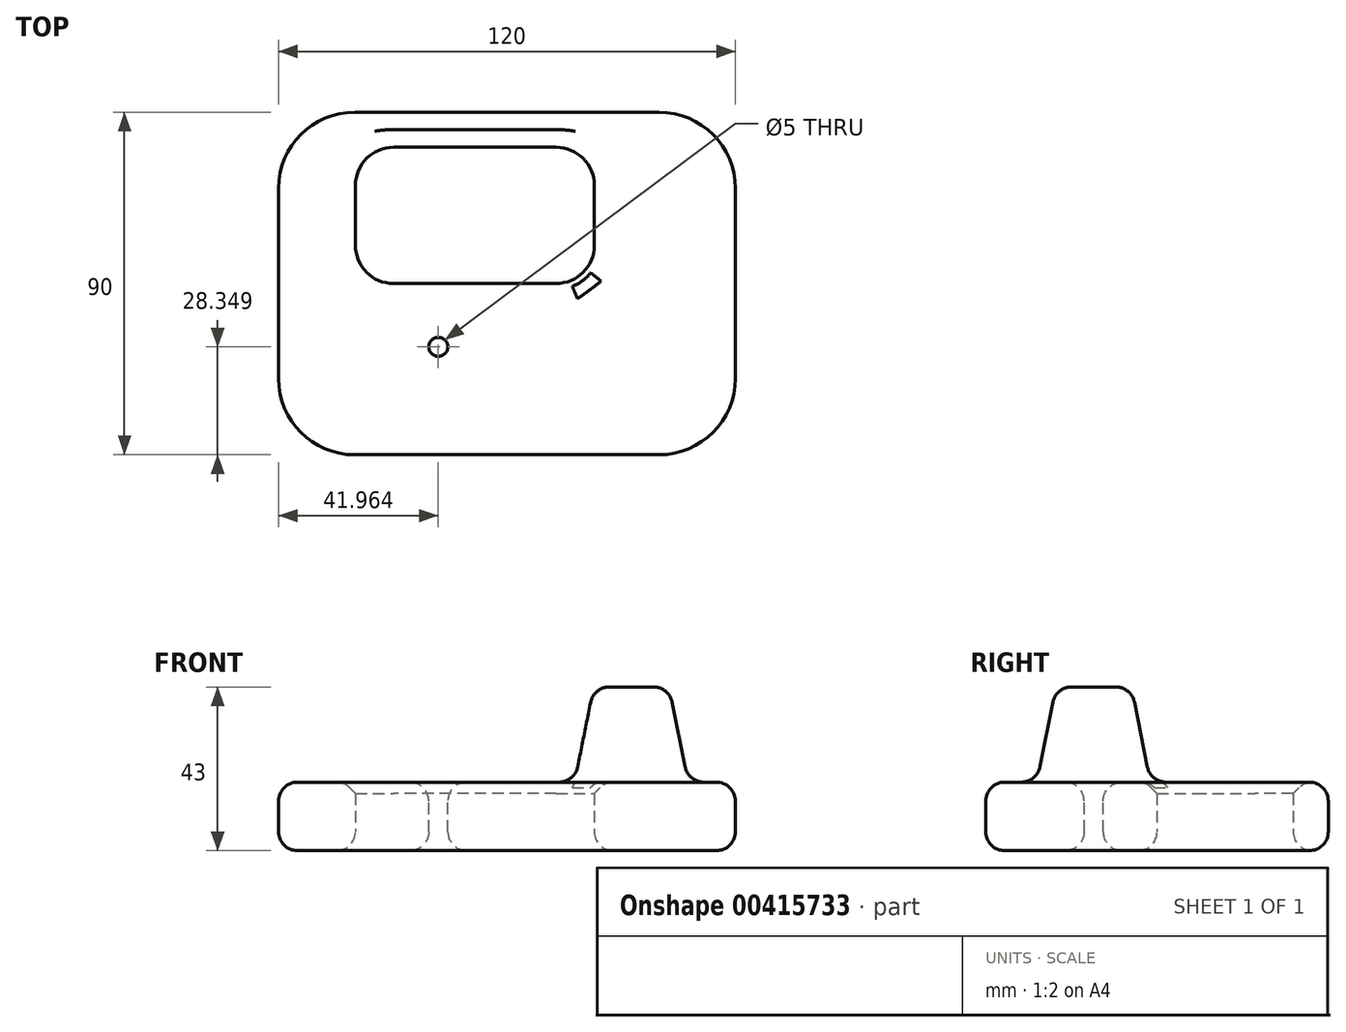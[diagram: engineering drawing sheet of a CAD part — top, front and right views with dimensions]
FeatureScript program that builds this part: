
annotation { "Feature Type Name" : "Feature", "Feature Type Description" : "" }
export const myFeature = defineFeature(function(context is Context, id is Id, definition is map)
    precondition{}
    {
        {
            var Q0;
            Q0=qCreatedBy(makeId("Top.planeOp"),FACE);
            var sketch = newSketch(context, id + "F0", { "sketchPlane" : qUnion([Q0])});
            skLineSegment(sketch, "E0.bottom", {"start": v(60, 45) * mm, "end": v(-60, 45) * mm});
            skLineSegment(sketch, "E0.top", {"start": v(60, -45) * mm, "end": v(-60, -45) * mm});
            skLineSegment(sketch, "E0.left", {"start": v(60, 45) * mm, "end": v(60, -45) * mm});
            skLineSegment(sketch, "E0.right", {"start": v(-60, 45) * mm, "end": v(-60, -45) * mm});
            skPoint(sketch, "E0.middle", {"position": v(0, 0) * mm});
            skSolve(sketch);
        }
        {
            var Q0;
            Q0=makeQuery(id+"F0.imprint","IMPRINT",FACE,{"disambiguationData":[TD([[makeQuery(id+"F0.imprint","IMPRINT",EDGE,{"derivedFrom":sQuery(id+"F0.wireOp",EDGE,"E0.bottom")}),1.0]])]});
            extrude(context, id + "F1", {"entities" : qUnion([Q0]), "depth" : 18 * mm});
        }
        {
            var Q0;
            Q0=qCreatedBy(makeId("Top.planeOp"),FACE);
            var sketch = newSketch(context, id + "F2", { "sketchPlane" : qUnion([Q0])});
            skLineSegment(sketch, "E1.bottom", {"start": v(22.95, 35.77) * mm, "end": v(-39.8, 35.77) * mm});
            skLineSegment(sketch, "E1.top", {"start": v(22.95, 0) * mm, "end": v(-39.8, 0) * mm});
            skLineSegment(sketch, "E1.left", {"start": v(22.95, 35.77) * mm, "end": v(22.95, 0) * mm});
            skLineSegment(sketch, "E1.right", {"start": v(-39.8, 35.77) * mm, "end": v(-39.8, 0) * mm});
            skSolve(sketch);
        }
        {
            var Q0;
            Q0=makeQuery(id+"F1.opExtrude","CAP_FACE",FACE,{"disambiguationData":[OSD([sQuery(id+"F0.wireOp",EDGE,"E0.bottom"),sQuery(id+"F0.wireOp",EDGE,"E0.top"),sQuery(id+"F0.wireOp",EDGE,"E0.left"),sQuery(id+"F0.wireOp",EDGE,"E0.right")])],"isStart":false});
            var Q1;
            Q1=makeQuery(id+"F2.imprint","IMPRINT",FACE,{"disambiguationData":[TD([[makeQuery(id+"F2.imprint","IMPRINT",EDGE,{"derivedFrom":sQuery(id+"F2.wireOp",EDGE,"E1.bottom")}),1.0]])]});
            extrude(context, id + "F3", {"entities" : qUnion([Q0, Q1]), "operationType" : NewBodyOperationType.REMOVE, "depth" : 20 * mm});
        }
        {
            var Q0;
            Q0=makeQuery(id+"F3.boolean.opBoolean","COPY",EDGE,{"derivedFrom":makeQuery(id+"F3.opExtrude","SWEPT_EDGE",EDGE,{"disambiguationData":[OSD([sQuery(id+"F2.wireOp",EDGE,"E1.bottom"),sQuery(id+"F2.wireOp",EDGE,"E1.left")])]})});
            var Q1;
            {var subQ0=sQuery(id+"F0.wireOp",EDGE,"E0.right");var subQ1=sQuery(id+"F0.wireOp",EDGE,"E0.left");var subQ2=sQuery(id+"F0.wireOp",EDGE,"E0.top");var subQ3=sQuery(id+"F0.wireOp",EDGE,"E0.bottom");var subQ4=makeQuery(id+"F1.opExtrude","CAP_FACE",FACE,{"disambiguationData":[OSD([subQ3,subQ2,subQ1,subQ0])],"isStart":false});var subQ5=makeQuery(id+"F3.opExtrude","CAP_FACE",FACE,{"disambiguationData":[OSD([subQ3,subQ2,subQ1,subQ0])],"isStart":true});Q1=makeQuery(id+"FmhjPb4m4sN7J4q_1.opFillet","BLEND_EDGE",EDGE,{"blendedFrom":[makeQuery(id+"F3.boolean.opBoolean","INTERSECT",EDGE,{"disambiguationData":[topologyDisambiguationEdgeConnected([makeQuery(id+"F3.opExtrude","SWEPT_FACE",FACE,{"disambiguationData":[OSD([sQuery(id+"F2.wireOp",EDGE,"E1.bottom")])]})])],"derivedFrom":[subQ4,subQ5]}),makeQuery(id+"F3.boolean.opBoolean","INTERSECT",EDGE,{"disambiguationData":[topologyDisambiguationEdgeConnected([makeQuery(id+"F3.opExtrude","SWEPT_FACE",FACE,{"disambiguationData":[OSD([sQuery(id+"F2.wireOp",EDGE,"E1.left")])]})])],"derivedFrom":[subQ4,subQ5]})],"blendedInto":[]});}
            var Q2;
            Q2=makeQuery(id+"F3.boolean.opBoolean","COPY",EDGE,{"derivedFrom":makeQuery(id+"F3.opExtrude","SWEPT_EDGE",EDGE,{"disambiguationData":[OSD([sQuery(id+"F2.wireOp",EDGE,"E1.bottom"),sQuery(id+"F2.wireOp",EDGE,"E1.right")])]})});
            var Q3;
            {var subQ0=sQuery(id+"F0.wireOp",EDGE,"E0.right");var subQ1=sQuery(id+"F0.wireOp",EDGE,"E0.left");var subQ2=sQuery(id+"F0.wireOp",EDGE,"E0.top");var subQ3=sQuery(id+"F0.wireOp",EDGE,"E0.bottom");var subQ4=makeQuery(id+"F1.opExtrude","CAP_FACE",FACE,{"disambiguationData":[OSD([subQ3,subQ2,subQ1,subQ0])],"isStart":false});var subQ5=makeQuery(id+"F3.opExtrude","CAP_FACE",FACE,{"disambiguationData":[OSD([subQ3,subQ2,subQ1,subQ0])],"isStart":true});Q3=makeQuery(id+"FmhjPb4m4sN7J4q_1.opFillet","BLEND_EDGE",EDGE,{"blendedFrom":[makeQuery(id+"F3.boolean.opBoolean","INTERSECT",EDGE,{"disambiguationData":[topologyDisambiguationEdgeConnected([makeQuery(id+"F3.opExtrude","SWEPT_FACE",FACE,{"disambiguationData":[OSD([sQuery(id+"F2.wireOp",EDGE,"E1.bottom")])]})])],"derivedFrom":[subQ4,subQ5]}),makeQuery(id+"F3.boolean.opBoolean","INTERSECT",EDGE,{"disambiguationData":[topologyDisambiguationEdgeConnected([makeQuery(id+"F3.opExtrude","SWEPT_FACE",FACE,{"disambiguationData":[OSD([sQuery(id+"F2.wireOp",EDGE,"E1.right")])]})])],"derivedFrom":[subQ4,subQ5]})],"blendedInto":[]});}
            var Q4;
            Q4=makeQuery(id+"F3.boolean.opBoolean","COPY",EDGE,{"derivedFrom":makeQuery(id+"F3.opExtrude","SWEPT_EDGE",EDGE,{"disambiguationData":[OSD([sQuery(id+"F2.wireOp",EDGE,"E1.top"),sQuery(id+"F2.wireOp",EDGE,"E1.right")])]})});
            var Q5;
            {var subQ0=sQuery(id+"F0.wireOp",EDGE,"E0.right");var subQ1=sQuery(id+"F0.wireOp",EDGE,"E0.left");var subQ2=sQuery(id+"F0.wireOp",EDGE,"E0.top");var subQ3=sQuery(id+"F0.wireOp",EDGE,"E0.bottom");var subQ4=makeQuery(id+"F1.opExtrude","CAP_FACE",FACE,{"disambiguationData":[OSD([subQ3,subQ2,subQ1,subQ0])],"isStart":false});var subQ5=makeQuery(id+"F3.opExtrude","CAP_FACE",FACE,{"disambiguationData":[OSD([subQ3,subQ2,subQ1,subQ0])],"isStart":true});Q5=makeQuery(id+"FmhjPb4m4sN7J4q_1.opFillet","BLEND_EDGE",EDGE,{"blendedFrom":[makeQuery(id+"F3.boolean.opBoolean","INTERSECT",EDGE,{"disambiguationData":[topologyDisambiguationEdgeConnected([makeQuery(id+"F3.opExtrude","SWEPT_FACE",FACE,{"disambiguationData":[OSD([sQuery(id+"F2.wireOp",EDGE,"E1.top")])]})])],"derivedFrom":[subQ4,subQ5]}),makeQuery(id+"F3.boolean.opBoolean","INTERSECT",EDGE,{"disambiguationData":[topologyDisambiguationEdgeConnected([makeQuery(id+"F3.opExtrude","SWEPT_FACE",FACE,{"disambiguationData":[OSD([sQuery(id+"F2.wireOp",EDGE,"E1.right")])]})])],"derivedFrom":[subQ4,subQ5]})],"blendedInto":[]});}
            var Q6;
            Q6=makeQuery(id+"F3.boolean.opBoolean","COPY",EDGE,{"derivedFrom":makeQuery(id+"F3.opExtrude","SWEPT_EDGE",EDGE,{"disambiguationData":[OSD([sQuery(id+"F2.wireOp",EDGE,"E1.top"),sQuery(id+"F2.wireOp",EDGE,"E1.left")])]})});
            var Q7;
            {var subQ0=sQuery(id+"F0.wireOp",EDGE,"E0.right");var subQ1=sQuery(id+"F0.wireOp",EDGE,"E0.left");var subQ2=sQuery(id+"F0.wireOp",EDGE,"E0.top");var subQ3=sQuery(id+"F0.wireOp",EDGE,"E0.bottom");var subQ4=makeQuery(id+"F1.opExtrude","CAP_FACE",FACE,{"disambiguationData":[OSD([subQ3,subQ2,subQ1,subQ0])],"isStart":false});var subQ5=makeQuery(id+"F3.opExtrude","CAP_FACE",FACE,{"disambiguationData":[OSD([subQ3,subQ2,subQ1,subQ0])],"isStart":true});Q7=makeQuery(id+"FmhjPb4m4sN7J4q_1.opFillet","BLEND_EDGE",EDGE,{"blendedFrom":[makeQuery(id+"F3.boolean.opBoolean","INTERSECT",EDGE,{"disambiguationData":[topologyDisambiguationEdgeConnected([makeQuery(id+"F3.opExtrude","SWEPT_FACE",FACE,{"disambiguationData":[OSD([sQuery(id+"F2.wireOp",EDGE,"E1.top")])]})])],"derivedFrom":[subQ4,subQ5]}),makeQuery(id+"F3.boolean.opBoolean","INTERSECT",EDGE,{"disambiguationData":[topologyDisambiguationEdgeConnected([makeQuery(id+"F3.opExtrude","SWEPT_FACE",FACE,{"disambiguationData":[OSD([sQuery(id+"F2.wireOp",EDGE,"E1.left")])]})])],"derivedFrom":[subQ4,subQ5]})],"blendedInto":[]});}
            fillet(context, id + "F4", {"entities" : qUnion([Q0, Q1, Q2, Q3, Q4, Q5, Q6, Q7]), "radius" : 10 * mm, "tangentPropagation" : true, "allowEdgeOverflow" : false});
        }
        {
            var Q0;
            Q0=makeQuery(id+"F1.opExtrude","SWEPT_EDGE",EDGE,{"disambiguationData":[OSD([sQuery(id+"F0.wireOp",EDGE,"E0.top"),sQuery(id+"F0.wireOp",EDGE,"E0.right")])]});
            var Q1;
            Q1=makeQuery(id+"F1.opExtrude","SWEPT_EDGE",EDGE,{"disambiguationData":[OSD([sQuery(id+"F0.wireOp",EDGE,"E0.bottom"),sQuery(id+"F0.wireOp",EDGE,"E0.right")])]});
            var Q2;
            Q2=makeQuery(id+"F1.opExtrude","SWEPT_EDGE",EDGE,{"disambiguationData":[OSD([sQuery(id+"F0.wireOp",EDGE,"E0.top"),sQuery(id+"F0.wireOp",EDGE,"E0.left")])]});
            var Q3;
            Q3=makeQuery(id+"F1.opExtrude","SWEPT_EDGE",EDGE,{"disambiguationData":[OSD([sQuery(id+"F0.wireOp",EDGE,"E0.bottom"),sQuery(id+"F0.wireOp",EDGE,"E0.left")])]});
            fillet(context, id + "F5", {"entities" : qUnion([Q0, Q1, Q2, Q3]), "radius" : 20 * mm, "tangentPropagation" : true, "allowEdgeOverflow" : false});
        }
        {
            var Q0;
            {var subQ0=sQuery(id+"F0.wireOp",EDGE,"E0.right");var subQ1=sQuery(id+"F0.wireOp",EDGE,"E0.left");var subQ2=sQuery(id+"F0.wireOp",EDGE,"E0.top");var subQ3=sQuery(id+"F0.wireOp",EDGE,"E0.bottom");var subQ4=makeQuery(id+"F1.opExtrude","CAP_FACE",FACE,{"disambiguationData":[OSD([subQ3,subQ2,subQ1,subQ0])],"isStart":false});Q0=makeQuery(id+"F3.boolean.opBoolean","INTERSECT",EDGE,{"disambiguationData":[topologyDisambiguationEdgeConnected([makeQuery(id+"F3.opExtrude","SWEPT_FACE",FACE,{"disambiguationData":[OSD([sQuery(id+"F2.wireOp",EDGE,"E1.bottom")])]})])],"derivedFrom":[subQ4,makeQuery(id+"F3.opExtrude","CAP_FACE",FACE,{"disambiguationData":[OSD([subQ3,subQ2,subQ1,subQ0])],"isStart":true})]});}
            var Q1;
            Q1=makeQuery(id+"F4.opFillet","BLEND_EDGE",EDGE,{"blendedFrom":[makeQuery(id+"F3.boolean.opBoolean","COPY",EDGE,{"derivedFrom":makeQuery(id+"F3.opExtrude","SWEPT_EDGE",EDGE,{"disambiguationData":[OSD([sQuery(id+"F2.wireOp",EDGE,"E1.bottom"),sQuery(id+"F2.wireOp",EDGE,"E1.left")])]})}),makeQuery(id+"F1.opExtrude","CAP_FACE",FACE,{"disambiguationData":[OSD([sQuery(id+"F0.wireOp",EDGE,"E0.bottom"),sQuery(id+"F0.wireOp",EDGE,"E0.top"),sQuery(id+"F0.wireOp",EDGE,"E0.left"),sQuery(id+"F0.wireOp",EDGE,"E0.right")])],"isStart":false})],"blendedInto":[makeQuery(id+"F1.opExtrude","CAP_FACE",FACE,{"disambiguationData":[OSD([sQuery(id+"F0.wireOp",EDGE,"E0.bottom"),sQuery(id+"F0.wireOp",EDGE,"E0.top"),sQuery(id+"F0.wireOp",EDGE,"E0.left"),sQuery(id+"F0.wireOp",EDGE,"E0.right")])],"isStart":false})]});
            var Q2;
            {var subQ0=sQuery(id+"F0.wireOp",EDGE,"E0.right");var subQ1=sQuery(id+"F0.wireOp",EDGE,"E0.left");var subQ2=sQuery(id+"F0.wireOp",EDGE,"E0.top");var subQ3=sQuery(id+"F0.wireOp",EDGE,"E0.bottom");var subQ4=makeQuery(id+"F1.opExtrude","CAP_FACE",FACE,{"disambiguationData":[OSD([subQ3,subQ2,subQ1,subQ0])],"isStart":false});Q2=makeQuery(id+"F3.boolean.opBoolean","INTERSECT",EDGE,{"disambiguationData":[topologyDisambiguationEdgeConnected([makeQuery(id+"F3.opExtrude","SWEPT_FACE",FACE,{"disambiguationData":[OSD([sQuery(id+"F2.wireOp",EDGE,"E1.left")])]})])],"derivedFrom":[subQ4,makeQuery(id+"F3.opExtrude","CAP_FACE",FACE,{"disambiguationData":[OSD([subQ3,subQ2,subQ1,subQ0])],"isStart":true})]});}
            var Q3;
            Q3=makeQuery(id+"F4.opFillet","BLEND_EDGE",EDGE,{"blendedFrom":[makeQuery(id+"F3.boolean.opBoolean","COPY",EDGE,{"derivedFrom":makeQuery(id+"F3.opExtrude","SWEPT_EDGE",EDGE,{"disambiguationData":[OSD([sQuery(id+"F2.wireOp",EDGE,"E1.top"),sQuery(id+"F2.wireOp",EDGE,"E1.left")])]})}),makeQuery(id+"F1.opExtrude","CAP_FACE",FACE,{"disambiguationData":[OSD([sQuery(id+"F0.wireOp",EDGE,"E0.bottom"),sQuery(id+"F0.wireOp",EDGE,"E0.top"),sQuery(id+"F0.wireOp",EDGE,"E0.left"),sQuery(id+"F0.wireOp",EDGE,"E0.right")])],"isStart":false})],"blendedInto":[makeQuery(id+"F1.opExtrude","CAP_FACE",FACE,{"disambiguationData":[OSD([sQuery(id+"F0.wireOp",EDGE,"E0.bottom"),sQuery(id+"F0.wireOp",EDGE,"E0.top"),sQuery(id+"F0.wireOp",EDGE,"E0.left"),sQuery(id+"F0.wireOp",EDGE,"E0.right")])],"isStart":false})]});
            var Q4;
            {var subQ0=sQuery(id+"F0.wireOp",EDGE,"E0.right");var subQ1=sQuery(id+"F0.wireOp",EDGE,"E0.left");var subQ2=sQuery(id+"F0.wireOp",EDGE,"E0.top");var subQ3=sQuery(id+"F0.wireOp",EDGE,"E0.bottom");var subQ4=makeQuery(id+"F1.opExtrude","CAP_FACE",FACE,{"disambiguationData":[OSD([subQ3,subQ2,subQ1,subQ0])],"isStart":false});Q4=makeQuery(id+"F3.boolean.opBoolean","INTERSECT",EDGE,{"disambiguationData":[topologyDisambiguationEdgeConnected([makeQuery(id+"F3.opExtrude","SWEPT_FACE",FACE,{"disambiguationData":[OSD([sQuery(id+"F2.wireOp",EDGE,"E1.top")])]})])],"derivedFrom":[subQ4,makeQuery(id+"F3.opExtrude","CAP_FACE",FACE,{"disambiguationData":[OSD([subQ3,subQ2,subQ1,subQ0])],"isStart":true})]});}
            var Q5;
            {var subQ0=sQuery(id+"F0.wireOp",EDGE,"E0.right");var subQ1=sQuery(id+"F0.wireOp",EDGE,"E0.left");var subQ2=sQuery(id+"F0.wireOp",EDGE,"E0.top");var subQ3=sQuery(id+"F0.wireOp",EDGE,"E0.bottom");var subQ4=makeQuery(id+"F1.opExtrude","CAP_FACE",FACE,{"disambiguationData":[OSD([subQ3,subQ2,subQ1,subQ0])],"isStart":false});Q5=makeQuery(id+"F3.boolean.opBoolean","INTERSECT",EDGE,{"disambiguationData":[topologyDisambiguationEdgeConnected([makeQuery(id+"F3.opExtrude","SWEPT_FACE",FACE,{"disambiguationData":[OSD([sQuery(id+"F2.wireOp",EDGE,"E1.right")])]})])],"derivedFrom":[subQ4,makeQuery(id+"F3.opExtrude","CAP_FACE",FACE,{"disambiguationData":[OSD([subQ3,subQ2,subQ1,subQ0])],"isStart":true})]});}
            var Q6;
            Q6=makeQuery(id+"F4.opFillet","BLEND_EDGE",EDGE,{"blendedFrom":[makeQuery(id+"F3.boolean.opBoolean","COPY",EDGE,{"derivedFrom":makeQuery(id+"F3.opExtrude","SWEPT_EDGE",EDGE,{"disambiguationData":[OSD([sQuery(id+"F2.wireOp",EDGE,"E1.top"),sQuery(id+"F2.wireOp",EDGE,"E1.right")])]})}),makeQuery(id+"F1.opExtrude","CAP_FACE",FACE,{"disambiguationData":[OSD([sQuery(id+"F0.wireOp",EDGE,"E0.bottom"),sQuery(id+"F0.wireOp",EDGE,"E0.top"),sQuery(id+"F0.wireOp",EDGE,"E0.left"),sQuery(id+"F0.wireOp",EDGE,"E0.right")])],"isStart":false})],"blendedInto":[makeQuery(id+"F1.opExtrude","CAP_FACE",FACE,{"disambiguationData":[OSD([sQuery(id+"F0.wireOp",EDGE,"E0.bottom"),sQuery(id+"F0.wireOp",EDGE,"E0.top"),sQuery(id+"F0.wireOp",EDGE,"E0.left"),sQuery(id+"F0.wireOp",EDGE,"E0.right")])],"isStart":false})]});
            var Q7;
            Q7=makeQuery(id+"F4.opFillet","BLEND_EDGE",EDGE,{"blendedFrom":[makeQuery(id+"F3.boolean.opBoolean","COPY",EDGE,{"derivedFrom":makeQuery(id+"F3.opExtrude","SWEPT_EDGE",EDGE,{"disambiguationData":[OSD([sQuery(id+"F2.wireOp",EDGE,"E1.bottom"),sQuery(id+"F2.wireOp",EDGE,"E1.right")])]})}),makeQuery(id+"F1.opExtrude","CAP_FACE",FACE,{"disambiguationData":[OSD([sQuery(id+"F0.wireOp",EDGE,"E0.bottom"),sQuery(id+"F0.wireOp",EDGE,"E0.top"),sQuery(id+"F0.wireOp",EDGE,"E0.left"),sQuery(id+"F0.wireOp",EDGE,"E0.right")])],"isStart":false})],"blendedInto":[makeQuery(id+"F1.opExtrude","CAP_FACE",FACE,{"disambiguationData":[OSD([sQuery(id+"F0.wireOp",EDGE,"E0.bottom"),sQuery(id+"F0.wireOp",EDGE,"E0.top"),sQuery(id+"F0.wireOp",EDGE,"E0.left"),sQuery(id+"F0.wireOp",EDGE,"E0.right")])],"isStart":false})]});
            chamfer(context, id + "F6", {"entities" : qUnion([Q0, Q1, Q2, Q3, Q4, Q5, Q6, Q7]), "width" : 3 * mm, "tangentPropagation" : true});
        }
        {
            var Q0;
            Q0=makeQuery(id+"F1.opExtrude","CAP_FACE",FACE,{"disambiguationData":[OSD([sQuery(id+"F0.wireOp",EDGE,"E0.bottom"),sQuery(id+"F0.wireOp",EDGE,"E0.top"),sQuery(id+"F0.wireOp",EDGE,"E0.left"),sQuery(id+"F0.wireOp",EDGE,"E0.right")])],"isStart":false});
            var sketch = newSketch(context, id + "F7", { "sketchPlane" : qUnion([Q0])});
            skCircle(sketch, "E2", {"center": v(32.7, -16.65) * mm, "radius": 14.92 * mm});
            skCircle(sketch, "E3", {"center": v(-18.04, -16.65) * mm, "radius": 7.58 * mm});
            skSolve(sketch);
        }
        {
            var Q0;
            Q0=sQuery(id+"F7.wireOp",VERTEX,"E3.center");
            var Q1;
            Q1=makeQuery(id+"F1.opExtrude","SWEPT_BODY",BODY,{"disambiguationData":[OSD([sQuery(id+"F0.wireOp",EDGE,"E0.bottom"),sQuery(id+"F0.wireOp",EDGE,"E0.top"),sQuery(id+"F0.wireOp",EDGE,"E0.left"),sQuery(id+"F0.wireOp",EDGE,"E0.right")])]});
            hole(context, id + "F8", {"style" : HoleStyle.SIMPLE, "endStyle" : HoleEndStyle.THROUGH, "holeDiameter" : 5 * mm, "isTappedThrough" : true, "tappedDepth" : 12 * mm, "tapClearance" : 3, "locations" : qUnion([Q0]), "scope" : qUnion([Q1])});
        }
        {
            var Q0;
            Q0=makeQuery(id+"F7.imprint","IMPRINT",FACE,{"disambiguationData":[TD([[makeQuery(id+"F7.imprint","IMPRINT",EDGE,{"derivedFrom":sQuery(id+"F7.wireOp",EDGE,"E2")}),1.0]])]});
            extrude(context, id + "F9", {"entities" : qUnion([Q0]), "operationType" : NewBodyOperationType.ADD, "depth" : 25 * mm});
        }
        {
            var Q0;
            Q0=makeQuery(id+"F9.opExtrude","CAP_EDGE",EDGE,{"disambiguationData":[OSD([sQuery(id+"F7.wireOp",EDGE,"E2")])],"isStart":false});
            chamfer(context, id + "F10", {"entities" : qUnion([Q0]), "chamferType" : ChamferType.TWO_OFFSETS, "width1" : 5 * mm, "oppositeDirection" : false, "width2" : 25 * mm, "tangentPropagation" : true});
        }
        {
            var Q0;
            {var subQ0=sQuery(id+"F7.wireOp",EDGE,"E2");Q0=makeQuery(id+"F10.opChamfer","BLEND_EDGE",EDGE,{"blendedFrom":[makeQuery(id+"F9.opExtrude","CAP_EDGE",EDGE,{"disambiguationData":[OSD([subQ0])],"isStart":false}),makeQuery(id+"F9.opExtrude","CAP_FACE",FACE,{"disambiguationData":[OSD([subQ0])],"isStart":false})],"blendedInto":[makeQuery(id+"F9.opExtrude","CAP_FACE",FACE,{"disambiguationData":[OSD([subQ0])],"isStart":false})]});}
            fillet(context, id + "F11", {"entities" : qUnion([Q0]), "radius" : 5 * mm, "tangentPropagation" : true, "allowEdgeOverflow" : false});
        }
        {
            var Q0;
            Q0=makeQuery(id+"F10.opChamfer","BLEND_EDGE",EDGE,{"blendedFrom":[makeQuery(id+"F9.opExtrude","CAP_EDGE",EDGE,{"disambiguationData":[OSD([sQuery(id+"F7.wireOp",EDGE,"E2")])],"isStart":false}),makeQuery(id+"F1.opExtrude","CAP_FACE",FACE,{"disambiguationData":[OSD([sQuery(id+"F0.wireOp",EDGE,"E0.bottom"),sQuery(id+"F0.wireOp",EDGE,"E0.top"),sQuery(id+"F0.wireOp",EDGE,"E0.left"),sQuery(id+"F0.wireOp",EDGE,"E0.right")])],"isStart":false})],"blendedInto":[makeQuery(id+"F1.opExtrude","CAP_FACE",FACE,{"disambiguationData":[OSD([sQuery(id+"F0.wireOp",EDGE,"E0.bottom"),sQuery(id+"F0.wireOp",EDGE,"E0.top"),sQuery(id+"F0.wireOp",EDGE,"E0.left"),sQuery(id+"F0.wireOp",EDGE,"E0.right")])],"isStart":false})]});
            fillet(context, id + "F12", {"entities" : qUnion([Q0]), "radius" : 5 * mm, "tangentPropagation" : true, "allowEdgeOverflow" : false});
        }
        {
            var Q0;
            Q0=makeQuery(id+"F1.opExtrude","CAP_FACE",FACE,{"disambiguationData":[OSD([sQuery(id+"F0.wireOp",EDGE,"E0.bottom"),sQuery(id+"F0.wireOp",EDGE,"E0.top"),sQuery(id+"F0.wireOp",EDGE,"E0.left"),sQuery(id+"F0.wireOp",EDGE,"E0.right")])],"isStart":false});
            fillet(context, id + "F13", {"entities" : qUnion([Q0]), "radius" : 5 * mm, "tangentPropagation" : true, "allowEdgeOverflow" : false});
        }
        {
            var Q0;
            Q0=makeQuery(id+"F1.opExtrude","CAP_FACE",FACE,{"disambiguationData":[OSD([sQuery(id+"F0.wireOp",EDGE,"E0.bottom"),sQuery(id+"F0.wireOp",EDGE,"E0.top"),sQuery(id+"F0.wireOp",EDGE,"E0.left"),sQuery(id+"F0.wireOp",EDGE,"E0.right")])],"isStart":true});
            fillet(context, id + "F14", {"entities" : qUnion([Q0]), "radius" : 5 * mm, "tangentPropagation" : true, "allowEdgeOverflow" : false});
        }
    });
